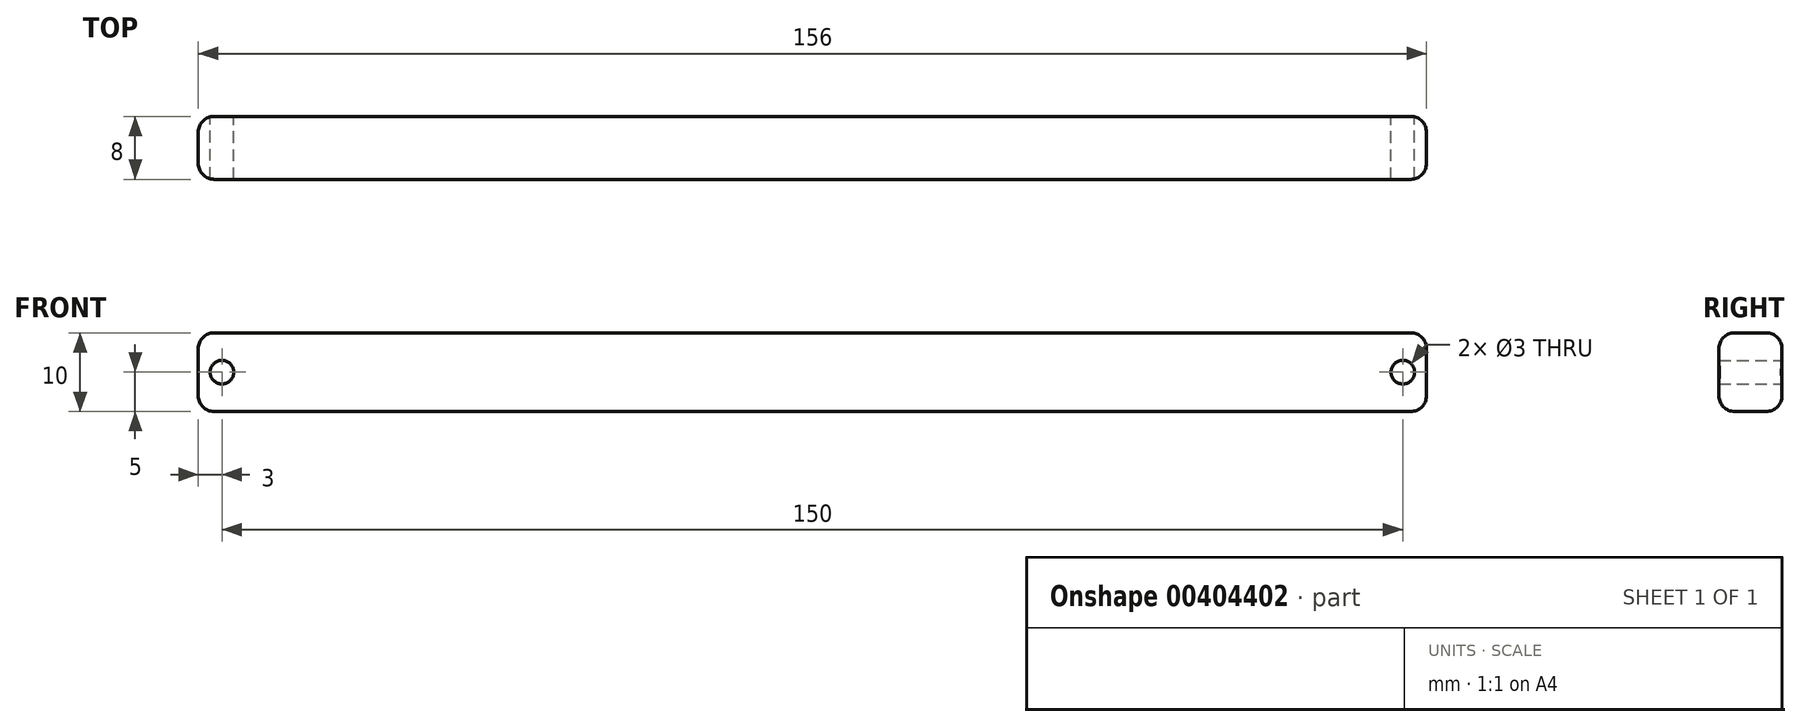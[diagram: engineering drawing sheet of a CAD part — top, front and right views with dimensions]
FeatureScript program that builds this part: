
annotation { "Feature Type Name" : "Feature", "Feature Type Description" : "" }
export const myFeature = defineFeature(function(context is Context, id is Id, definition is map)
    precondition{}
    {
        {
            var Q0;
            Q0=qCreatedBy(makeId("Front.planeOp"),FACE);
            var sketch = newSketch(context, id + "F0", { "sketchPlane" : qUnion([Q0])});
            skLineSegment(sketch, "E0.bottom", {"start": v(-103, 0) * mm, "end": v(53, 0) * mm});
            skLineSegment(sketch, "E0.top", {"start": v(-103, 10) * mm, "end": v(53, 10) * mm});
            skLineSegment(sketch, "E0.left", {"start": v(-103, 0) * mm, "end": v(-103, 10) * mm});
            skLineSegment(sketch, "E0.right", {"start": v(53, 0) * mm, "end": v(53, 10) * mm});
            skCircle(sketch, "E1", {"center": v(50, 5) * mm, "radius": 1.5 * mm});
            skCircle(sketch, "E2.1.0.0", {"center": v(-100, 5) * mm, "radius": 1.5 * mm});
            skLineSegment(sketch, "E2.direction1", {"start": v(50, 5) * mm, "end": v(-100, 5) * mm, "construction": true});
            skSolve(sketch);
        }
        {
            var Q0;
            Q0=makeQuery(id+"F0.imprint","IMPRINT",FACE,{"disambiguationData":[TD([[makeQuery(id+"F0.imprint","IMPRINT",EDGE,{"derivedFrom":sQuery(id+"F0.wireOp",EDGE,"E0.bottom")}),1.0]])]});
            var Q1;
            Q1=sQuery(id+"F0.wireOp",EDGE,"E0.top");
            extrude(context, id + "F1", {"entities" : qUnion([Q0]), "surfaceEntities" : qUnion([Q1]), "depth" : 8 * mm});
        }
        {
            var Q0;
            Q0=makeQuery(id+"F1.opExtrude","SWEPT_FACE",FACE,{"disambiguationData":[OSD([sQuery(id+"F0.wireOp",EDGE,"E0.top")])]});
            var Q1;
            Q1=makeQuery(id+"F1.opExtrude","SWEPT_FACE",FACE,{"disambiguationData":[OSD([sQuery(id+"F0.wireOp",EDGE,"E0.right")])]});
            fillet(context, id + "F2", {"entities" : qUnion([Q0, Q1]), "radius" : 2 * mm, "tangentPropagation" : true, "allowEdgeOverflow" : false});
        }
        {
            var Q0;
            Q0=makeQuery(id+"F1.opExtrude","SWEPT_FACE",FACE,{"disambiguationData":[OSD([sQuery(id+"F0.wireOp",EDGE,"E0.left")])]});
            var Q1;
            Q1=makeQuery(id+"F1.opExtrude","SWEPT_FACE",FACE,{"disambiguationData":[OSD([sQuery(id+"F0.wireOp",EDGE,"E0.bottom")])]});
            fillet(context, id + "F3", {"entities" : qUnion([Q0, Q1]), "radius" : 2 * mm, "tangentPropagation" : true, "allowEdgeOverflow" : false});
        }
    });
